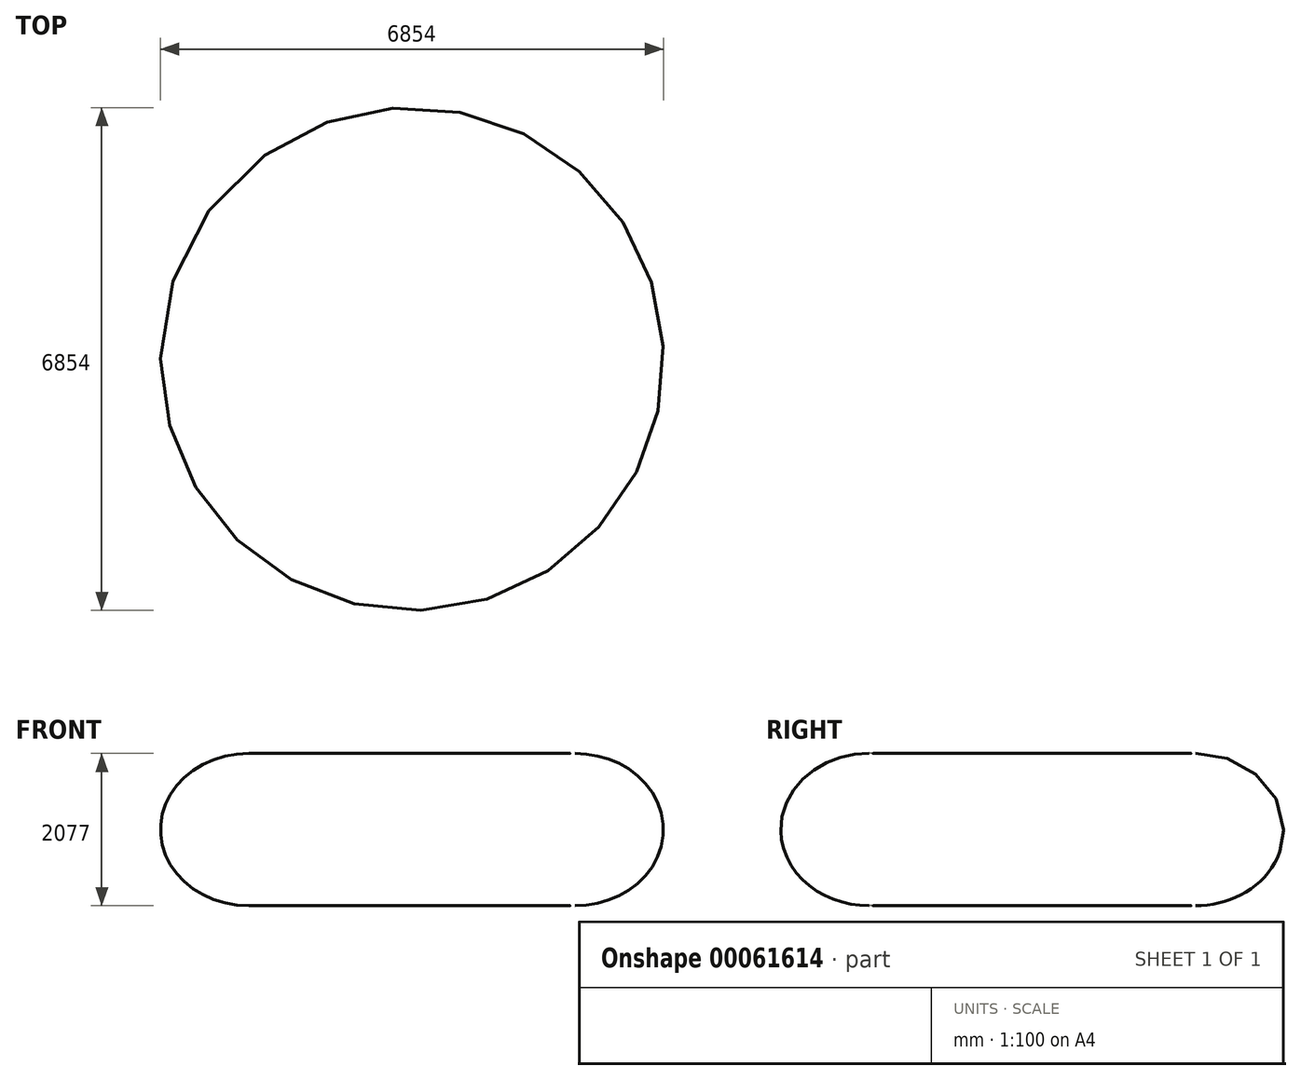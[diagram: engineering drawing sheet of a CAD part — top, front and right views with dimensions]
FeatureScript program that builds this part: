
annotation { "Feature Type Name" : "Feature", "Feature Type Description" : "" }
export const myFeature = defineFeature(function(context is Context, id is Id, definition is map)
    precondition{}
    {
        {
            var Q0;
            Q0=qCreatedBy(makeId("Front.planeOp"),FACE);
            var sketch = newSketch(context, id + "F0", { "sketchPlane" : qUnion([Q0])});
            skLineSegment(sketch, "E0", {"start": v(0, 0) * mm, "end": v(-2225, 0) * mm});
            skPoint(sketch, "E1", {"position": v(-2225, 1038.5) * mm});
            skEllipticalArc(sketch, "E2", {});
            skPoint(sketch, "E3", {"position": v(-2225, 2077) * mm});
            skPoint(sketch, "E4", {"position": v(-3427, 1038.5) * mm});
            skPoint(sketch, "E5", {"position": v(-2225, 0) * mm});
            skLineSegment(sketch, "E6", {"start": v(-2225, 2077) * mm, "end": v(0, 2077) * mm});
            skLineSegment(sketch, "E7", {"start": v(0, 2077) * mm, "end": v(0, 0) * mm});
            const initialGuessF0  = {"E2": [-2.225, 1.0385, -1, 0, 1.202, 1.0385, 4.71238898038469, 1.5707963267948966]};
            skSetInitialGuess(sketch, initialGuessF0);
            skSolve(sketch);
        }
        {
            var Q0;
            Q0=qCreatedBy(makeId("Front.planeOp"),FACE);
            var sketch = newSketch(context, id + "F1", { "sketchPlane" : qUnion([Q0])});
            skLineSegment(sketch, "E8", {"start": v(0, 0) * mm, "end": v(0, 2077) * mm});
            skSolve(sketch);
        }
        {
            var Q0;
            Q0 = qSketchRegion(id + "F0", true);
            var Q1;
            Q1 = qConstructionFilter(qBodyType(qCreatedBy(id + "F0" ,EDGE), BodyType.WIRE), ConstructionObject.NO);
            var Q2;
            Q2=sQuery(id+"F1.wireOp",EDGE,"E8");
            revolve(context, id + "F2", {"entities" : qUnion([Q0]), "surfaceEntities" : qUnion([Q1]), "axis" : qUnion([Q2]), "revolveType" : RevolveType.FULL});
        }
    });
